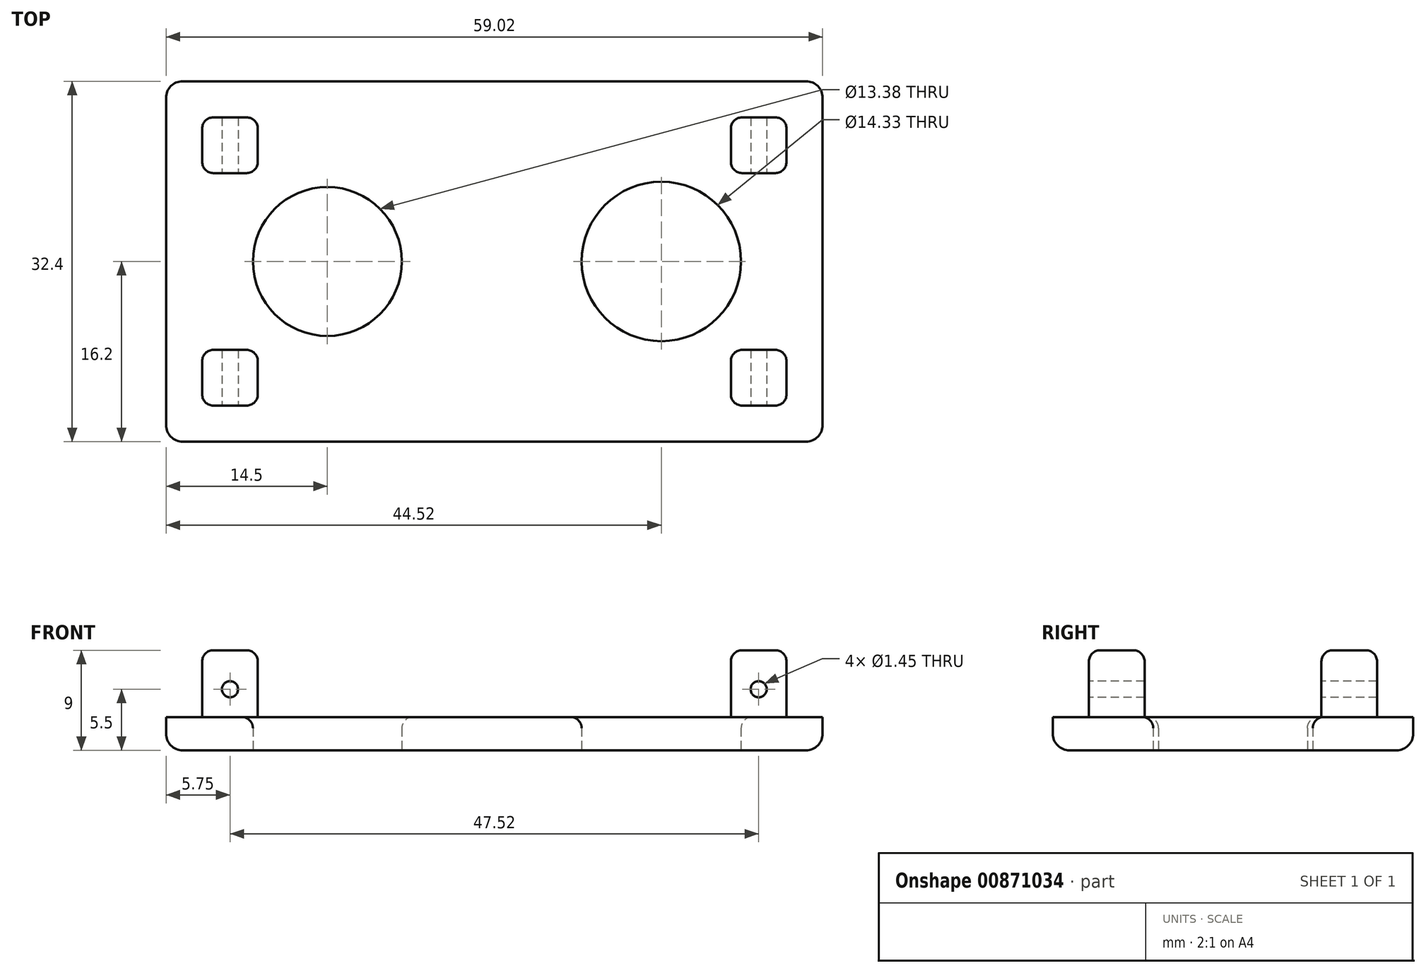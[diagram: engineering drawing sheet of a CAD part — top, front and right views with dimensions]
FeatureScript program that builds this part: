
annotation { "Feature Type Name" : "Feature", "Feature Type Description" : "" }
export const myFeature = defineFeature(function(context is Context, id is Id, definition is map)
    precondition{}
    {
        {
            var Q0;
            Q0=qCreatedBy(makeId("Top.planeOp"),FACE);
            var sketch = newSketch(context, id + "F0", { "sketchPlane" : qUnion([Q0])});
            skLineSegment(sketch, "E0.bottom", {"start": v(29.51, -16.2) * mm, "end": v(-29.5, -16.2) * mm});
            skLineSegment(sketch, "E0.top", {"start": v(29.51, 16.2) * mm, "end": v(-29.51, 16.2) * mm});
            skLineSegment(sketch, "E0.left", {"start": v(29.51, -16.2) * mm, "end": v(29.51, 16.2) * mm});
            skLineSegment(sketch, "E0.right", {"start": v(-29.5, -16.2) * mm, "end": v(-29.51, 16.2) * mm});
            skPoint(sketch, "E0.middle", {"position": v(0, 0) * mm});
            skCircle(sketch, "E1", {"center": v(-15, 0) * mm, "radius": 6.7 * mm});
            skCircle(sketch, "E2", {"center": v(15.01, 0) * mm, "radius": 7.16 * mm});
            skSolve(sketch);
        }
        {
            var Q0;
            Q0=makeQuery(id+"F0.imprint","IMPRINT",FACE,{"disambiguationData":[TD([[makeQuery(id+"F0.imprint","IMPRINT",EDGE,{"derivedFrom":sQuery(id+"F0.wireOp",EDGE,"E0.bottom")}),-1.0]])]});
            extrude(context, id + "F1", {"entities" : qUnion([Q0]), "endBound" : BoundingType.SYMMETRIC, "depth" : 3 * mm, "offsetDistance" : 25 * mm});
        }
        {
            var Q0;
            Q0=makeQuery(id+"F1.opExtrude","CAP_FACE",FACE,{"disambiguationData":[OSD([sQuery(id+"F0.wireOp",EDGE,"E0.bottom"),sQuery(id+"F0.wireOp",EDGE,"E0.top"),sQuery(id+"F0.wireOp",EDGE,"E0.left"),sQuery(id+"F0.wireOp",EDGE,"E0.right"),sQuery(id+"F0.wireOp",EDGE,"E1"),sQuery(id+"F0.wireOp",EDGE,"E2")])],"isStart":false});
            var sketch = newSketch(context, id + "F2", { "sketchPlane" : qUnion([Q0])});
            skLineSegment(sketch, "E3.bottom", {"start": v(-26.26, 12.95) * mm, "end": v(-21.26, 12.95) * mm});
            skLineSegment(sketch, "E3.top", {"start": v(-26.26, 7.95) * mm, "end": v(-21.26, 7.95) * mm});
            skLineSegment(sketch, "E3.left", {"start": v(-26.26, 12.95) * mm, "end": v(-26.26, 7.95) * mm});
            skLineSegment(sketch, "E3.right", {"start": v(-21.26, 12.95) * mm, "end": v(-21.26, 7.95) * mm});
            skLineSegment(sketch, "E4.bottom", {"start": v(21.26, 12.95) * mm, "end": v(26.26, 12.95) * mm});
            skLineSegment(sketch, "E4.top", {"start": v(21.26, 7.95) * mm, "end": v(26.26, 7.95) * mm});
            skLineSegment(sketch, "E4.left", {"start": v(21.26, 12.95) * mm, "end": v(21.26, 7.95) * mm});
            skLineSegment(sketch, "E4.right", {"start": v(26.26, 12.95) * mm, "end": v(26.26, 7.95) * mm});
            skLineSegment(sketch, "E5.bottom", {"start": v(-26.26, -7.95) * mm, "end": v(-21.26, -7.95) * mm});
            skLineSegment(sketch, "E5.top", {"start": v(-26.26, -12.95) * mm, "end": v(-21.26, -12.95) * mm});
            skLineSegment(sketch, "E5.left", {"start": v(-26.26, -7.95) * mm, "end": v(-26.26, -12.95) * mm});
            skLineSegment(sketch, "E5.right", {"start": v(-21.26, -7.95) * mm, "end": v(-21.26, -12.95) * mm});
            skLineSegment(sketch, "E6.bottom", {"start": v(21.26, -7.95) * mm, "end": v(26.26, -7.95) * mm});
            skLineSegment(sketch, "E6.top", {"start": v(21.26, -12.95) * mm, "end": v(26.26, -12.95) * mm});
            skLineSegment(sketch, "E6.left", {"start": v(21.26, -7.95) * mm, "end": v(21.26, -12.95) * mm});
            skLineSegment(sketch, "E6.right", {"start": v(26.26, -7.95) * mm, "end": v(26.26, -12.95) * mm});
            skSolve(sketch);
        }
        {
            var Q0;
            Q0=makeQuery(id+"F2.imprint","IMPRINT",FACE,{"disambiguationData":[TD([[makeQuery(id+"F2.imprint","IMPRINT",EDGE,{"derivedFrom":sQuery(id+"F2.wireOp",EDGE,"E5.bottom")}),-1.0]])]});
            var Q1;
            Q1=makeQuery(id+"F2.imprint","IMPRINT",FACE,{"disambiguationData":[TD([[makeQuery(id+"F2.imprint","IMPRINT",EDGE,{"derivedFrom":sQuery(id+"F2.wireOp",EDGE,"E3.bottom")}),-1.0]])]});
            var Q2;
            Q2=makeQuery(id+"F2.imprint","IMPRINT",FACE,{"disambiguationData":[TD([[makeQuery(id+"F2.imprint","IMPRINT",EDGE,{"derivedFrom":sQuery(id+"F2.wireOp",EDGE,"E4.bottom")}),-1.0]])]});
            var Q3;
            Q3=makeQuery(id+"F2.imprint","IMPRINT",FACE,{"disambiguationData":[TD([[makeQuery(id+"F2.imprint","IMPRINT",EDGE,{"derivedFrom":sQuery(id+"F2.wireOp",EDGE,"E6.bottom")}),-1.0]])]});
            extrude(context, id + "F3", {"entities" : qUnion([Q0, Q1, Q2, Q3]), "operationType" : NewBodyOperationType.ADD, "depth" : 6 * mm, "offsetDistance" : 25 * mm});
        }
        {
            var Q0;
            Q0=makeQuery(id+"F3.opExtrude","SWEPT_EDGE",EDGE,{"disambiguationData":[OSD([sQuery(id+"F2.wireOp",EDGE,"E6.top"),sQuery(id+"F2.wireOp",EDGE,"E6.right")])]});
            var Q1;
            Q1=makeQuery(id+"F3.opExtrude","SWEPT_EDGE",EDGE,{"disambiguationData":[OSD([sQuery(id+"F2.wireOp",EDGE,"E6.bottom"),sQuery(id+"F2.wireOp",EDGE,"E6.right")])]});
            var Q2;
            Q2=makeQuery(id+"F3.opExtrude","SWEPT_EDGE",EDGE,{"disambiguationData":[OSD([sQuery(id+"F2.wireOp",EDGE,"E4.top"),sQuery(id+"F2.wireOp",EDGE,"E4.right")])]});
            var Q3;
            Q3=makeQuery(id+"F3.opExtrude","SWEPT_EDGE",EDGE,{"disambiguationData":[OSD([sQuery(id+"F2.wireOp",EDGE,"E4.bottom"),sQuery(id+"F2.wireOp",EDGE,"E4.right")])]});
            var Q4;
            Q4=makeQuery(id+"F3.opExtrude","SWEPT_EDGE",EDGE,{"disambiguationData":[OSD([sQuery(id+"F2.wireOp",EDGE,"E6.top"),sQuery(id+"F2.wireOp",EDGE,"E6.left")])]});
            var Q5;
            Q5=makeQuery(id+"F3.opExtrude","SWEPT_EDGE",EDGE,{"disambiguationData":[OSD([sQuery(id+"F2.wireOp",EDGE,"E6.bottom"),sQuery(id+"F2.wireOp",EDGE,"E6.left")])]});
            var Q6;
            Q6=makeQuery(id+"F3.opExtrude","SWEPT_EDGE",EDGE,{"disambiguationData":[OSD([sQuery(id+"F2.wireOp",EDGE,"E5.top"),sQuery(id+"F2.wireOp",EDGE,"E5.right")])]});
            var Q7;
            Q7=makeQuery(id+"F3.opExtrude","SWEPT_EDGE",EDGE,{"disambiguationData":[OSD([sQuery(id+"F2.wireOp",EDGE,"E5.top"),sQuery(id+"F2.wireOp",EDGE,"E5.left")])]});
            var Q8;
            Q8=makeQuery(id+"F3.opExtrude","SWEPT_EDGE",EDGE,{"disambiguationData":[OSD([sQuery(id+"F2.wireOp",EDGE,"E5.bottom"),sQuery(id+"F2.wireOp",EDGE,"E5.left")])]});
            var Q9;
            Q9=makeQuery(id+"F3.opExtrude","SWEPT_EDGE",EDGE,{"disambiguationData":[OSD([sQuery(id+"F2.wireOp",EDGE,"E3.top"),sQuery(id+"F2.wireOp",EDGE,"E3.left")])]});
            var Q10;
            Q10=makeQuery(id+"F3.opExtrude","SWEPT_EDGE",EDGE,{"disambiguationData":[OSD([sQuery(id+"F2.wireOp",EDGE,"E3.top"),sQuery(id+"F2.wireOp",EDGE,"E3.right")])]});
            var Q11;
            Q11=makeQuery(id+"F3.opExtrude","SWEPT_EDGE",EDGE,{"disambiguationData":[OSD([sQuery(id+"F2.wireOp",EDGE,"E4.bottom"),sQuery(id+"F2.wireOp",EDGE,"E4.left")])]});
            var Q12;
            Q12=makeQuery(id+"F3.opExtrude","SWEPT_EDGE",EDGE,{"disambiguationData":[OSD([sQuery(id+"F2.wireOp",EDGE,"E4.top"),sQuery(id+"F2.wireOp",EDGE,"E4.left")])]});
            var Q13;
            Q13=makeQuery(id+"F3.opExtrude","SWEPT_EDGE",EDGE,{"disambiguationData":[OSD([sQuery(id+"F2.wireOp",EDGE,"E3.bottom"),sQuery(id+"F2.wireOp",EDGE,"E3.left")])]});
            var Q14;
            Q14=makeQuery(id+"F3.opExtrude","SWEPT_EDGE",EDGE,{"disambiguationData":[OSD([sQuery(id+"F2.wireOp",EDGE,"E3.bottom"),sQuery(id+"F2.wireOp",EDGE,"E3.right")])]});
            var Q15;
            Q15=makeQuery(id+"F3.opExtrude","SWEPT_EDGE",EDGE,{"disambiguationData":[OSD([sQuery(id+"F2.wireOp",EDGE,"E5.bottom"),sQuery(id+"F2.wireOp",EDGE,"E5.right")])]});
            fillet(context, id + "F4", {"entities" : qUnion([Q0, Q1, Q2, Q3, Q4, Q5, Q6, Q7, Q8, Q9, Q10, Q11, Q12, Q13, Q14, Q15]), "radius" : 1 * mm, "tangentPropagation" : true, "allowEdgeOverflow" : false});
        }
        {
            var Q0;
            Q0=makeQuery(id+"F3.opExtrude","CAP_FACE",FACE,{"disambiguationData":[OSD([sQuery(id+"F2.wireOp",EDGE,"E5.bottom"),sQuery(id+"F2.wireOp",EDGE,"E5.top"),sQuery(id+"F2.wireOp",EDGE,"E5.left"),sQuery(id+"F2.wireOp",EDGE,"E5.right")])],"isStart":false});
            var Q1;
            Q1=makeQuery(id+"F3.opExtrude","CAP_FACE",FACE,{"disambiguationData":[OSD([sQuery(id+"F2.wireOp",EDGE,"E3.bottom"),sQuery(id+"F2.wireOp",EDGE,"E3.top"),sQuery(id+"F2.wireOp",EDGE,"E3.left"),sQuery(id+"F2.wireOp",EDGE,"E3.right")])],"isStart":false});
            var Q2;
            Q2=makeQuery(id+"F3.opExtrude","CAP_FACE",FACE,{"disambiguationData":[OSD([sQuery(id+"F2.wireOp",EDGE,"E4.bottom"),sQuery(id+"F2.wireOp",EDGE,"E4.top"),sQuery(id+"F2.wireOp",EDGE,"E4.left"),sQuery(id+"F2.wireOp",EDGE,"E4.right")])],"isStart":false});
            var Q3;
            Q3=makeQuery(id+"F3.opExtrude","CAP_FACE",FACE,{"disambiguationData":[OSD([sQuery(id+"F2.wireOp",EDGE,"E6.bottom"),sQuery(id+"F2.wireOp",EDGE,"E6.top"),sQuery(id+"F2.wireOp",EDGE,"E6.left"),sQuery(id+"F2.wireOp",EDGE,"E6.right")])],"isStart":false});
            var Q4;
            Q4=makeQuery(id+"F1.opExtrude","CAP_EDGE",EDGE,{"disambiguationData":[OSD([sQuery(id+"F0.wireOp",EDGE,"E2")])],"isStart":false});
            var Q5;
            Q5=makeQuery(id+"F1.opExtrude","CAP_EDGE",EDGE,{"disambiguationData":[OSD([sQuery(id+"F0.wireOp",EDGE,"E1")])],"isStart":false});
            fillet(context, id + "F5", {"entities" : qUnion([Q0, Q1, Q2, Q3, Q4, Q5]), "radius" : 1 * mm, "tangentPropagation" : true, "allowEdgeOverflow" : false});
        }
        {
            var Q0;
            Q0=makeQuery(id+"F1.opExtrude","CAP_EDGE",EDGE,{"disambiguationData":[OSD([sQuery(id+"F0.wireOp",EDGE,"E0.top")])],"isStart":true});
            var Q1;
            Q1=makeQuery(id+"F1.opExtrude","CAP_EDGE",EDGE,{"disambiguationData":[OSD([sQuery(id+"F0.wireOp",EDGE,"E0.right")])],"isStart":true});
            var Q2;
            Q2=makeQuery(id+"F1.opExtrude","CAP_EDGE",EDGE,{"disambiguationData":[OSD([sQuery(id+"F0.wireOp",EDGE,"E0.bottom")])],"isStart":true});
            var Q3;
            Q3=makeQuery(id+"F1.opExtrude","CAP_EDGE",EDGE,{"disambiguationData":[OSD([sQuery(id+"F0.wireOp",EDGE,"E0.left")])],"isStart":true});
            fillet(context, id + "F6", {"entities" : qUnion([Q0, Q1, Q2, Q3]), "radius" : 1.5 * mm, "tangentPropagation" : true, "allowEdgeOverflow" : false});
        }
        {
            var Q0;
            Q0=makeQuery(id+"F1.opExtrude","SWEPT_EDGE",EDGE,{"disambiguationData":[OSD([sQuery(id+"F0.wireOp",EDGE,"E0.top"),sQuery(id+"F0.wireOp",EDGE,"E0.left")])]});
            var Q1;
            Q1=makeQuery(id+"F1.opExtrude","SWEPT_EDGE",EDGE,{"disambiguationData":[OSD([sQuery(id+"F0.wireOp",EDGE,"E0.top"),sQuery(id+"F0.wireOp",EDGE,"E0.right")])]});
            var Q2;
            Q2=makeQuery(id+"F1.opExtrude","SWEPT_EDGE",EDGE,{"disambiguationData":[OSD([sQuery(id+"F0.wireOp",EDGE,"E0.bottom"),sQuery(id+"F0.wireOp",EDGE,"E0.right")])]});
            var Q3;
            Q3=makeQuery(id+"F1.opExtrude","SWEPT_EDGE",EDGE,{"disambiguationData":[OSD([sQuery(id+"F0.wireOp",EDGE,"E0.bottom"),sQuery(id+"F0.wireOp",EDGE,"E0.left")])]});
            fillet(context, id + "F7", {"entities" : qUnion([Q0, Q1, Q2, Q3]), "radius" : 1.5 * mm, "tangentPropagation" : true, "allowEdgeOverflow" : false});
        }
        {
            var Q0;
            Q0=makeQuery(id+"F3.opExtrude","SWEPT_FACE",FACE,{"disambiguationData":[OSD([sQuery(id+"F2.wireOp",EDGE,"E6.top")])]});
            var sketch = newSketch(context, id + "F8", { "sketchPlane" : qUnion([Q0])});
            skCircle(sketch, "E7", {"center": v(23.76, 4) * mm, "radius": 0.72 * mm});
            skSolve(sketch);
        }
        {
            var Q0;
            Q0 = qSketchRegion(id + "F8", true);
            extrude(context, id + "F9", {"entities" : qUnion([Q0]), "operationType" : NewBodyOperationType.REMOVE, "oppositeDirection" : true, "depth" : 35 * mm, "offsetDistance" : 25 * mm});
        }
        {
            var Q0;
            Q0=makeQuery(id+"F3.opExtrude","SWEPT_FACE",FACE,{"disambiguationData":[OSD([sQuery(id+"F2.wireOp",EDGE,"E5.top")])]});
            var sketch = newSketch(context, id + "F10", { "sketchPlane" : qUnion([Q0])});
            skCircle(sketch, "E8", {"center": v(-23.76, 4) * mm, "radius": 0.72 * mm});
            skSolve(sketch);
        }
        {
            var Q0;
            Q0 = qSketchRegion(id + "F10", true);
            extrude(context, id + "F11", {"entities" : qUnion([Q0]), "operationType" : NewBodyOperationType.REMOVE, "oppositeDirection" : true, "depth" : 35 * mm, "offsetDistance" : 25 * mm});
        }
    });
